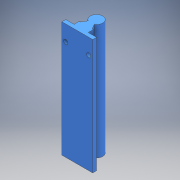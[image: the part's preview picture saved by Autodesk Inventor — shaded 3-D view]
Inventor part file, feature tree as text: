
AUTODESK INVENTOR PART (.ipt)
format: ipt  version: 2018 (Build 220112000, 112)  size: 141,312 bytes
history: native  units: mm
features: sketch x2, other x1, extrude x1, hole x1
ambient origin geometry x8: Origin, YZ Plane, XZ Plane, XY Plane, X Axis, Y Axis, Z Axis, Center Point
bodies: Body1 (feature_tree)
feature tree (5):
  other  "Sólido1"
  extrude  "Extrusão1"  Depth=25.0mm
  hole  "Furo1"  [1 undecoded]
  sketch  "Esboço1"  dims[d6=16.0mm d7=25.0mm]
  sketch  "Esboço3"  dims[d8=18.5mm d9=11.7mm d10=8.0mm d11=30.0deg d12=30.0deg d13=5.0mm d14=40.0mm d15=150.0mm d16=0.0mm d18=15.0mm d19=15.0mm d20=5.5mm d21=5.5mm d22=20.0mm d28=5.5mm d29=6.0mm d30=4.0mm d31=2.0mm d32=90.0deg d33=8.0mm d34=20.594885mm]
note: 1 required parameter value undecoded (feature->parameter linkage not recoverable at this tier; creation-order binding heuristic only, values carry confidence <= 0.55)
